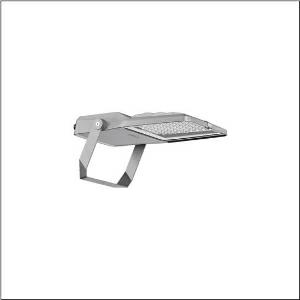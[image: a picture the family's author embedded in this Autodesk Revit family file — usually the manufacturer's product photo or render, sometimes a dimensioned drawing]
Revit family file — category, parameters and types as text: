
# Revit family: floodlight_fl_21_iq_mini___pl61_5xa7772d5c1a_2039
name_source: partatom
category: Lighting Fixtures
units: mm (PartAtom-declared; Revit-internal decimal feet)

## family parameters
Cut with Voids When Loaded = No
Host = Face
Light Source = No
Part Type = Normal
Room Calculation Point = No
Round Connector Dimension = Use Diameter
Shared = No

## types (1)
- --- (1 x LED, 16340 lm, 143 W, 4000K)
    Apparent Load = 143 VA
    CIE Flux Codes = 33 65 98 100 100
    Color Rendering = 80
    Color Temperature = 4000K
    Default Elevation = 1800 mm
    Description = Floodlight FL 21 iQ mini, floodlight, primary light control with lens, of PMMA, primary optical cover: protective disc, of toughened safety glass, transparent, light distribution: PL61, light emission: direct distribution, installation type: surface-mounted, LED, High Power LED, rated luminous flux: 16.340lm, luminous efficacy: 114lm/W, light colour: 840, colour temperature: 4000K, control gear: iQ Street-Remote/DALI, control: Street-Remote, Auto-Match, Temp-Guard, Night-Set, Smart-Wire, Desk-Remote (wireless, voltage-free reading and setting of iQ features in the workshop via application-optimized NFC function/RFID function), optimised constant luminous flux control (CLO 2.0), with terminal, 6-pole, mains connection: 220..240V, AC, 50/60Hz, start of lifetime: 143W, end of service life: 152W, reduction: 61W, luminaire housing, of diecast aluminium, powder-coated, Siteco® metallic grey (DB 702S), corrosivity category C5 mid according to DIN EN ISO 12944, suitable for swimming pools, chlorine-resistant, sealing non-destructively replaceable, mounting bracket, of steel, galvanised, powder-coated, Siteco® metallic grey (DB 702S), protection rating (complete): IP66, insulation class (complete): insulation class II (safety insulation), certification: CE, ENEC, VDE, protection symbol: D, impact resistance: IK08, permissible operating ambient temperature: -40..+40°C, permissible operating ambient temperature for outdoor applications: -40..+50°C, standard: DIN EN 12944, LABS conformity tested according to VDMA 24364:2018-05, packaging unit: 1 piece

Light Distribution: PL61
    Height = 70 mm
    Lamp = 1 x LED
    Lamp Light Flux = 16340 lm
    Lamp Power = 143 W
    Lamp count = 1
    Length = 485 mm
    Luminous efficacy = 114 lm/W
    Manufacturer = Siteco
    ModVariant = No
    Model = 5XA7772D5C1A
    Number of Poles = 1
    OnlyDefault = Yes
    Power Factor = 1
    Product Name = Floodlight FL 21 iQ mini | PL61
    Product group = floodlight | pylon annexe
    ProductGroupID = 6200
    Protection Class = Protection class II
    Protection Degree = IP 66
    RLX_Detail_Level = 1
    RLX_Emergency_Light_Flux = 0 lm
    RLX_Emergency_Type = 0
    RLX_Emergency_Type_DB = No
    RlxData = <blob elided: 96513 chars, md5=34fd7453>
    Socket = socket
    Standby Power = 0 W
    System Light Flux = 16340 lm
    System Power = 143 W
    Type Comments = factory setting: luminous flux: 100 % | dim-lin: 254 | 730 mA
    Type Image = l_1006845.jpg
    URL = http://relux.com
    VarID = @adj_172262
    Voltage = 0 V
    Weight = 0.00 kg
    Width = 337 mm

## geometry (parser evidence)
native form markers: Blend x4, Sweep x14
no freeform markers — native parametric forms only
